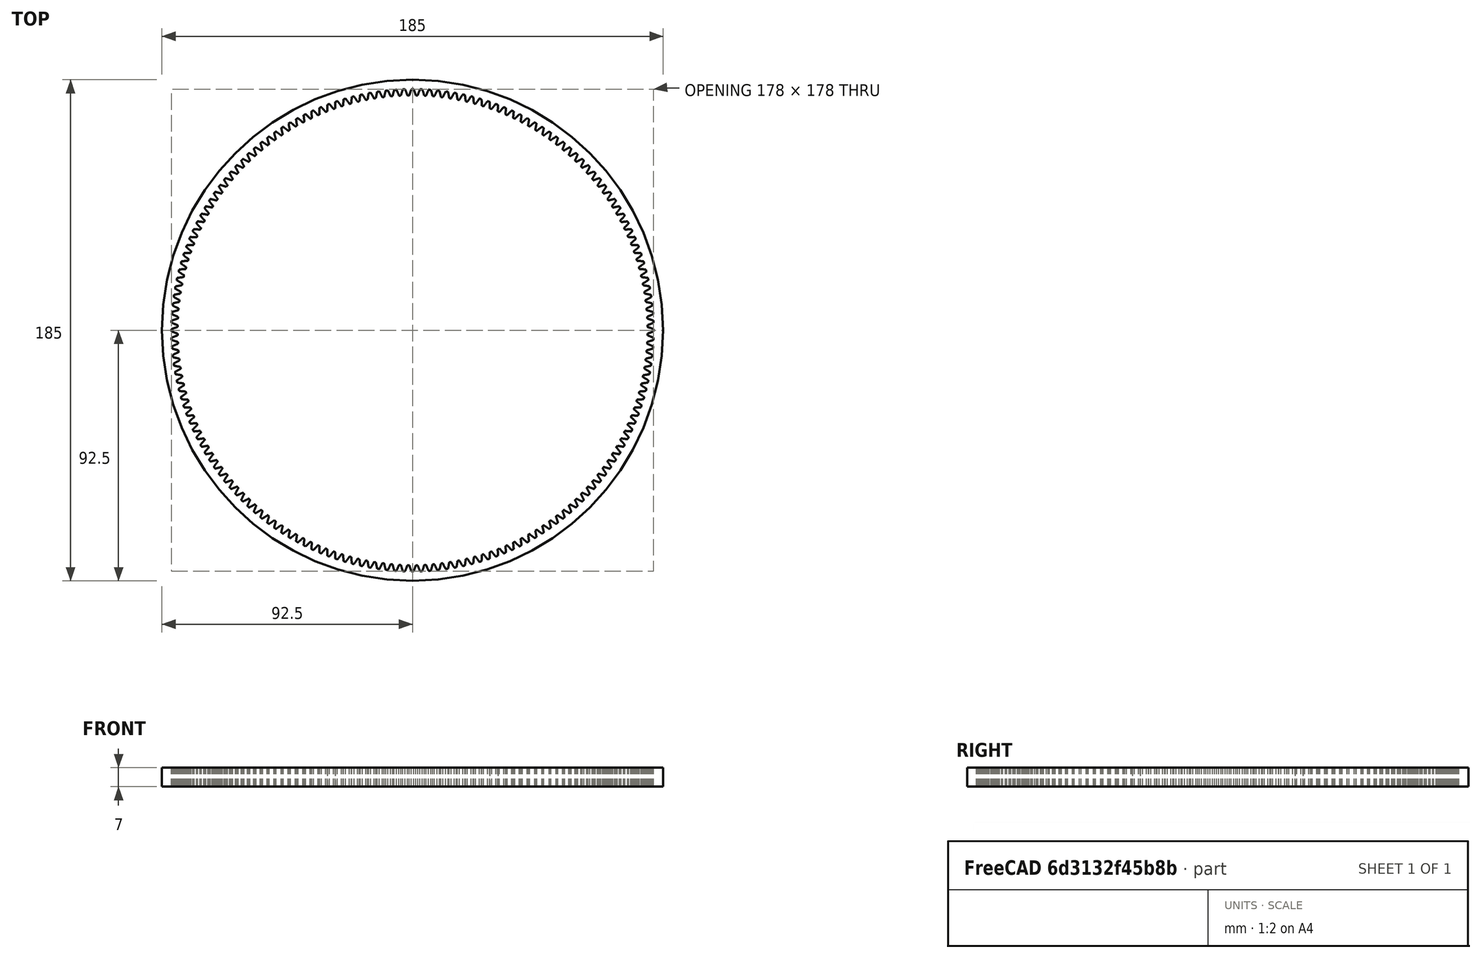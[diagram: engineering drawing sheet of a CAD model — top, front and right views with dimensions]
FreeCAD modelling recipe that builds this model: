
FCSTD DOCUMENT  (FreeCAD 0.19R24276 (Git))
Label: In_gear_t176_w7_cat_d185_A2
License: All rights reserved
LicenseURL: http://en.wikipedia.org/wiki/All_rights_reserved
objects: PartDesign::FeaturePython×1, PartDesign::Body×1, Part::Cylinder×1, Part::Cut×1
note: 4 computed .brp shape members not serialized (recipe doc carries the construction recipe); baked Part::Feature solids carry a one-line shape summary decoded from their .brp

FEATURE [PartDesign::FeaturePython] involutegear001  # WARN: FeaturePython — macro-defined, semantics opaque (R4)
  AttacherType = Attacher::AttachEngine3D
  backlash = 0
  beta = 0
  clearance = 0.25
  da = 178
  df = 173.5
  double_helix = false
  dw = 176
  head = 0
  height = 7
  module = 1
  numpoints = 6
  pressure_angle = 20
  properties_from_tool = false
  reversed_backlash = false
  shift = 0
  simple = false
  teeth = 176
  transverse_pitch = 3.14159
  undercut = false
  version = 0.0.3
FEATURE [PartDesign::Body] Body
  Group = -> [involutegear001]
  Origin = -> Origin
  Tip = -> involutegear001
FEATURE [Part::Cylinder] Cylinder  label="Цилиндр"
  Angle = 360
  AttacherType = Attacher::AttachEngine3D
  Height = 7
  Radius = 92.5
FEATURE [Part::Cut] Cut
  Base = -> Cylinder
  Tool = -> Body
